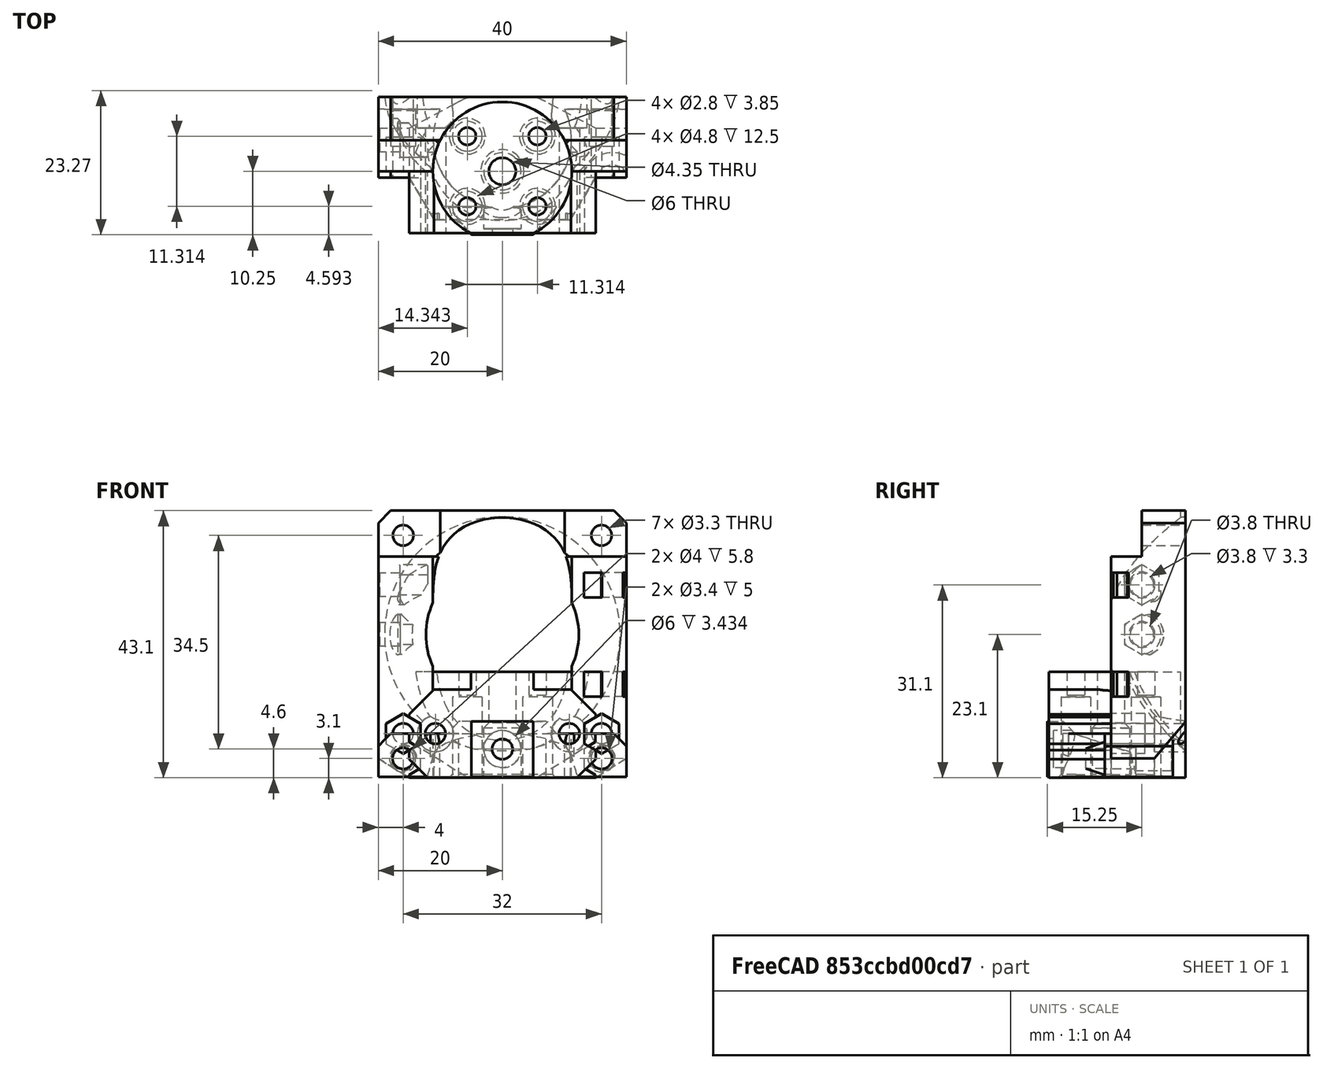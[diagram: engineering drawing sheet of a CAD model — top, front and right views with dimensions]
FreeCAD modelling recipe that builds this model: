
FCSTD DOCUMENT  (FreeCAD 0.19R24291 (Git))
Label: dragon-mount-thread-insert-mod
License: Other
LicenseURL: GPL3
objects: Part::Cylinder×8, Part::MultiFuse×8, Part::Chamfer×5, Part::Feature×2, Part::Cut×2, Part::Box×2
note: 27 computed .brp shape members not serialized (recipe doc carries the construction recipe); baked Part::Feature solids carry a one-line shape summary decoded from their .brp

FEATURE [Part::Feature] Part__Feature  label="dragon_face"
  Placement = pos=(0,34,79) rot=(0,0,1;0rad)
  shape: bbox 40.01 x 23.2 x 43.11 mm, 122 faces (baked)
FEATURE [Part::Cylinder] Cylinder
  Angle = 360
  AttacherType = Attacher::AttachEngine3D
  Height = 3.5
  Placement = pos=(-16.5,5,31) rot=(0,-1,0;1.5708rad)
  Radius = 1.9
FEATURE [Part::Cylinder] Cylinder001
  Angle = 360
  AttacherType = Attacher::AttachEngine3D
  Height = 3.5
  Placement = pos=(-16.5,5,23) rot=(0,-1,0;1.5708rad)
  Radius = 1.9
FEATURE [Part::Cylinder] Cylinder002
  Angle = 360
  AttacherType = Attacher::AttachEngine3D
  Height = 3.5
  Placement = pos=(-16.5,5,23) rot=(0,-1,0;1.5708rad)
  Radius = 3.5
FEATURE [Part::Cylinder] Cylinder003
  Angle = 360
  AttacherType = Attacher::AttachEngine3D
  Height = 3.5
  Placement = pos=(-16.5,5,31) rot=(0,-1,0;1.5708rad)
  Radius = 3.5
FEATURE [Part::MultiFuse] Fusion
  Shapes = -> [Cylinder003,Cylinder002]
FEATURE [Part::Chamfer] Chamfer
  Base = -> Fusion
  Edges = 2 edges r=0.4: [Edge3,Edge6]
FEATURE [Part::MultiFuse] Fusion001
  Shapes = -> [Cylinder001,Cylinder]
FEATURE [Part::MultiFuse] Fusion002
  Shapes = -> [Part__Feature,Chamfer]
FEATURE [Part::Cut] Cut
  Base = -> Fusion002
  Tool = -> Fusion001
FEATURE [Part::Chamfer] Chamfer001
  Base = -> Cut
  Edges = 2 edges r=0.2: [Edge231,Edge232]
FEATURE [Part::Feature] Part__Feature001  label="v6_support"
  Placement = pos=(0,39.2,43) rot=(0,0,1;0rad)
  shape: bbox 40 x 20.25 x 9.266 mm, 50 faces (baked)
FEATURE [Part::Box] Box  label="Cube"
  AttacherType = Attacher::AttachEngine3D
  Height = 7
  Length = 7
  Placement = pos=(12,-1,0) rot=(0,0,1;0rad)
  Width = 11
FEATURE [Part::Box] Box001  label="Cube001"
  AttacherType = Attacher::AttachEngine3D
  Height = 7
  Length = 7
  Placement = pos=(-19,-1,0) rot=(0,0,1;0rad)
  Width = 11
FEATURE [Part::MultiFuse] Fusion003
  Shapes = -> [Box001,Box]
FEATURE [Part::Chamfer] Chamfer002
  Base = -> Fusion003
  Edges = 2 edges r=1: [Edge2,Edge18]
FEATURE [Part::Cylinder] Cylinder004
  Angle = 360
  AttacherType = Attacher::AttachEngine3D
  Height = 15
  Placement = pos=(16,10,3) rot=(1,0,0;1.5708rad)
  Radius = 1.7
FEATURE [Part::Cylinder] Cylinder005
  Angle = 360
  AttacherType = Attacher::AttachEngine3D
  Height = 15
  Placement = pos=(-16,10,3) rot=(1,0,0;1.5708rad)
  Radius = 1.7
FEATURE [Part::Cylinder] Cylinder006
  Angle = 360
  AttacherType = Attacher::AttachEngine3D
  Height = 6
  Placement = pos=(16,10,3) rot=(1,0,0;1.5708rad)
  Radius = 2
FEATURE [Part::Cylinder] Cylinder007
  Angle = 360
  AttacherType = Attacher::AttachEngine3D
  Height = 6
  Placement = pos=(-16,10,3) rot=(1,0,0;1.5708rad)
  Radius = 2
FEATURE [Part::MultiFuse] Fusion004
  Shapes = -> [Cylinder004,Cylinder005]
FEATURE [Part::MultiFuse] Fusion005
  Shapes = -> [Cylinder006,Cylinder007]
FEATURE [Part::MultiFuse] Fusion006
  Shapes = -> [Fusion005,Fusion004]
FEATURE [Part::Chamfer] Chamfer003
  Base = -> Chamfer002
  Edges = 2 edges r=0.4: [Edge12,Edge26]
FEATURE [Part::MultiFuse] Fusion007
  Shapes = -> [Chamfer003,Part__Feature001]
FEATURE [Part::Cut] Cut001
  Base = -> Fusion007
  Tool = -> Fusion006
FEATURE [Part::Chamfer] Chamfer004
  Base = -> Cut001
  Edges = 2 edges r=0.2: [Edge121,Edge150]
